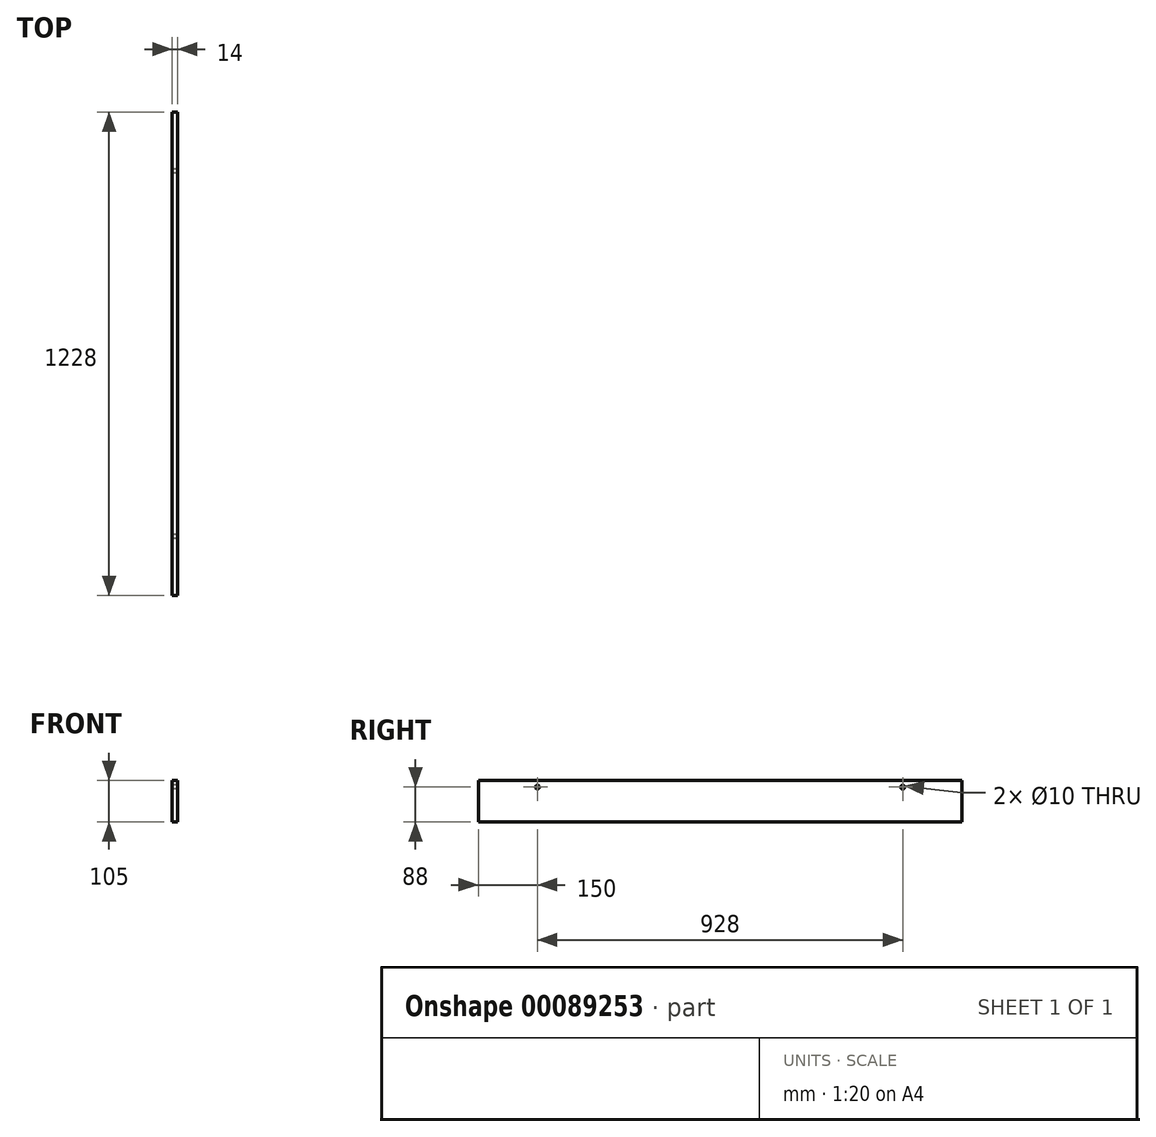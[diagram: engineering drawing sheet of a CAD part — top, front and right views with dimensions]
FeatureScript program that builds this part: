
annotation { "Feature Type Name" : "Feature", "Feature Type Description" : "" }
export const myFeature = defineFeature(function(context is Context, id is Id, definition is map)
    precondition{}
    {
        {
            var Q0;
            Q0=qCreatedBy(makeId("Front.planeOp"),FACE);
            var sketch = newSketch(context, id + "F0", { "sketchPlane" : qUnion([Q0])});
            skLineSegment(sketch, "E0.bottom", {"start": v(-7, 52.5) * mm, "end": v(7, 52.5) * mm});
            skLineSegment(sketch, "E0.top", {"start": v(-7, -52.5) * mm, "end": v(7, -52.5) * mm});
            skLineSegment(sketch, "E0.left", {"start": v(-7, 52.5) * mm, "end": v(-7, -52.5) * mm});
            skLineSegment(sketch, "E0.right", {"start": v(7, 52.5) * mm, "end": v(7, -52.5) * mm});
            skPoint(sketch, "E0.middle", {"position": v(0, 0) * mm});
            skSolve(sketch);
        }
        {
            var Q0;
            Q0=makeQuery(id+"F0.imprint","IMPRINT",FACE,{"disambiguationData":[TD([[makeQuery(id+"F0.imprint","IMPRINT",EDGE,{"derivedFrom":sQuery(id+"F0.wireOp",EDGE,"E0.bottom")}),-1.0]])]});
            extrude(context, id + "F1", {"entities" : qUnion([Q0]), "depth" : 1228 * mm});
        }
        {
            var Q0;
            Q0=makeQuery(id+"F1.opExtrude","SWEPT_FACE",FACE,{"disambiguationData":[OSD([sQuery(id+"F0.wireOp",EDGE,"E0.left")])]});
            var sketch = newSketch(context, id + "F2", { "sketchPlane" : qUnion([Q0])});
            skLineSegment(sketch, "E1.0.0", {"start": v(0, 52.5) * mm, "end": v(0, -52.5) * mm});
            skLineSegment(sketch, "E1.0.1", {"start": v(0, -52.5) * mm, "end": v(1228, -52.5) * mm});
            skLineSegment(sketch, "E1.0.2", {"start": v(1228, -52.5) * mm, "end": v(1228, 52.5) * mm});
            skLineSegment(sketch, "E1.0.3", {"start": v(1228, 52.5) * mm, "end": v(0, 52.5) * mm});
            skCircle(sketch, "E2", {"center": v(1078, 35.5) * mm, "radius": 5 * mm});
            skCircle(sketch, "E3", {"center": v(150, 35.5) * mm, "radius": 5 * mm});
            skSolve(sketch);
        }
        {
            var Q0;
            Q0=makeQuery(id+"F2.imprint","IMPRINT",FACE,{"disambiguationData":[TD([[makeQuery(id+"F2.imprint","IMPRINT",EDGE,{"derivedFrom":sQuery(id+"F2.wireOp",EDGE,"E3")}),1.0]])]});
            var Q1;
            Q1=makeQuery(id+"F2.imprint","IMPRINT",FACE,{"disambiguationData":[TD([[makeQuery(id+"F2.imprint","IMPRINT",EDGE,{"derivedFrom":sQuery(id+"F2.wireOp",EDGE,"E2")}),1.0]])]});
            extrude(context, id + "F3", {"entities" : qUnion([Q0, Q1]), "operationType" : NewBodyOperationType.REMOVE, "oppositeDirection" : true, "depth" : 25 * mm});
        }
    });
